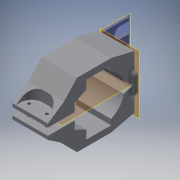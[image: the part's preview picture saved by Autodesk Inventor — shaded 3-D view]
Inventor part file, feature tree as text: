
AUTODESK INVENTOR PART (.ipt)
format: ipt  version: 2016 (Build 200138000, 138)  size: 439,296 bytes
history: native  units: in
note: dims shown in document units (in); Inventor stores cm internally (conversion verified against a paired STEP export)
features: sketch x12, extrude x11, projected_geometry x6, plane x4, reference x4, fillet x3, revolve x1
ambient origin geometry x8: Origin, YZ Plane, XZ Plane, XY Plane, X Axis, Y Axis, Z Axis, Center Point
bodies: Solid1 (feature_tree)
feature tree (41):
  plane  "Work Plane1"
  plane  "Work Plane2"
  extrude  "Extrusion1"  Depth=1.315in
  plane  "Work Plane3"
  extrude  "Extrusion2"  Depth=1.4in
  extrude  "Extrusion3"  Depth=1.8in TaperAngle=0.0deg
  plane  "Work Plane4"
  revolve  "Revolution1"  [1 undecoded]
  fillet  "Fillet1"  Radius=1.925in
  extrude  "Extrusion4"  TaperAngle=90.0deg  [1 undecoded]
  extrude  "Extrusion5"  Depth=0.2in TaperAngle=0.0deg
  extrude  "Extrusion6"  Depth=0.2in TaperAngle=0.0deg
  extrude  "Extrusion7"  Depth=2.575in TaperAngle=0.0deg
  extrude  "Extrusion8"  Depth=0.175in
  extrude  "Extrusion9"  Depth=0.2in TaperAngle=0.0deg
  fillet  "Fillet2"  Radius=0.2in
  fillet  "Fillet3"  Radius=0.625in
  extrude  "Extrusion10"  Depth=0.35in
  extrude  "Extrusion11"  Depth=0.2in
  sketch  "Sketch1"  dims[d2=0.6575in d3=1.315in]
  reference  "Reference1"
  sketch  "Sketch2"  dims[d10=2.92in d11=1.4in]
  sketch  "Sketch3"  dims[d12=0.35in d13=1.8in d14=0.0in]
  reference  "Reference2"
  sketch  "Sketch4"  dims[d15=0.5in d16=0.35in d17=1.925in d18=0.0in]
  reference  "Reference3"
  sketch  "Sketch5"  dims[d19=1.925in d20=0.0in d21=90.0deg]
  projected_geometry  "Projected Loop1"
  reference  "Reference4"
  sketch  "Sketch6"  dims[d22=0.3125in d23=0.2in d24=0.0in]
  projected_geometry  "Projected Loop2"
  sketch  "Sketch7"  dims[d25=1.5in d26=0.2in d27=0.0in]
  projected_geometry  "Projected Loop3"
  sketch  "Sketch8"  dims[d28=0.4in d29=2.575in d30=0.0in]
  projected_geometry  "Projected Loop4"
  sketch  "Sketch9"  dims[d31=0.175in d32=0.175in]
  sketch  "Sketch10"  dims[d33=2.575in d34=0.0in d35=0.2in d36=0.0in d37=0.2in d38=0.0in d39=0.625in]
  sketch  "Sketch11"  dims[d40=0.625in d41=0.35in]
  projected_geometry  "Projected Loop5"
  sketch  "Sketch12"  dims[d44=0.3in d45=0.2in d46=0.2in d47=0.4in d48=90.0deg d49=0.3in d50=10.0in d51=0.0in d52=0.2in d53=0.0in]
  projected_geometry  "Projected Loop6"
note: 2 required parameter values undecoded (feature->parameter linkage not recoverable at this tier; creation-order binding heuristic only, values carry confidence <= 0.55)